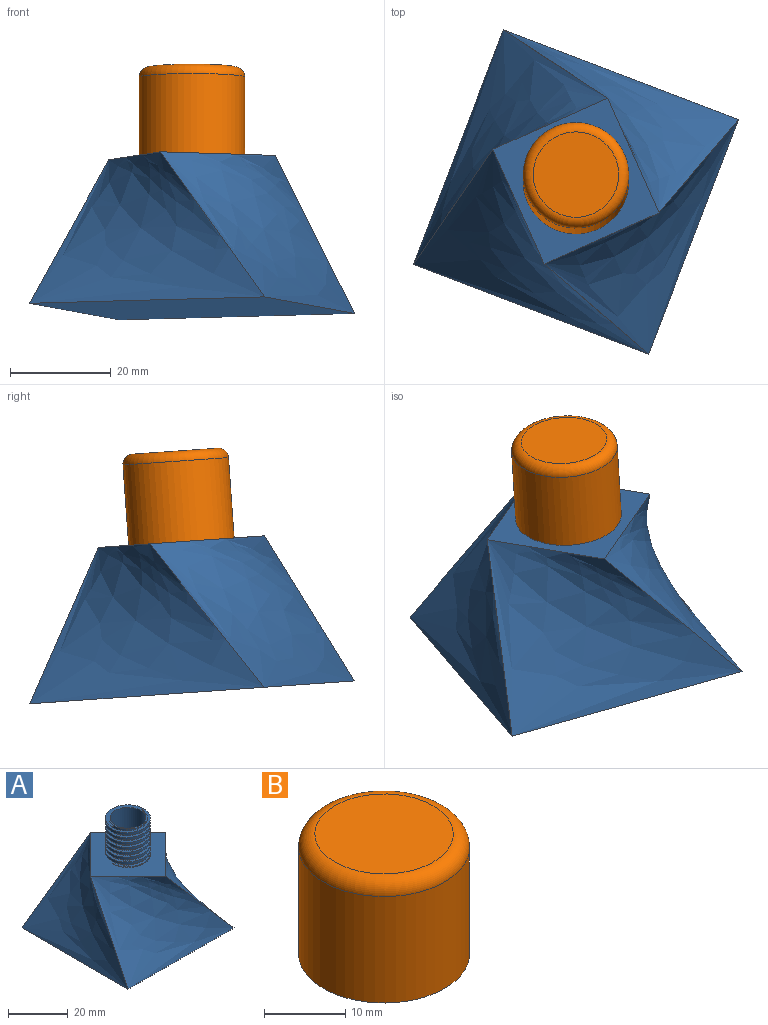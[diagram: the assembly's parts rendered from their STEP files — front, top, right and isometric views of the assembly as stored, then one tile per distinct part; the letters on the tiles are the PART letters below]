
ASSEMBLY  parts=2 mates=1
PART A: 18 faces, bbox 53x53x48 mm
  f0: cylinder r=7.5mm len=15mm, axis (0,0,-1), area 358.7mm2, adj f1,f3,f16,f17
  f1: plane 15x14mm, normal (0,0,1), area 41.6mm2, adj f0,f8,f15,f16,f17
  f2: plane 50x50mm, normal (0,0,-1), area 2500mm2, adj f4,f5,f6,f7
  f3: plane 35.36x35.36mm, normal (0,0,1), area 470.3mm2, adj f0,f4,f5,f6,f7,f15,f16,f17
  f4: bspline ~50x30mm, area 1200.4mm2, adj f2,f3,f5,f7
  f5: bspline ~50x30mm, area 1200.4mm2, adj f2,f3,f4,f6
  f6: bspline ~50x30mm, area 1200.4mm2, adj f2,f3,f5,f7
  f7: bspline ~50x30mm, area 1200.4mm2, adj f2,f3,f4,f6
  f8: cylinder r=6mm len=16.5mm, axis (0,0,-1), area 622mm2, adj f1,f10
  f9: plane 46.11x46.11mm, normal (0,0,1), area 2021.9mm2, adj f11,f12,f13,f14
  f10: plane 31.34x31.34mm, normal (0,0,-1), area 388.8mm2, adj f8,f11,f12,f13,f14
  f11: offset ~53x33mm, area 966.7mm2, adj f9,f10,f12,f14
  f12: offset ~53x33mm, area 966.7mm2, adj f9,f10,f11,f13
  f13: offset ~53x33mm, area 966.7mm2, adj f9,f10,f12,f14
  f14: offset ~53x33mm, area 966.7mm2, adj f9,f10,f11,f13
  f15: cylinder r=6.5mm len=15mm, axis (0,0,1), area 310.9mm2, adj f1,f3,f16,f17
  f16: bspline ~17.32x15.33mm, area 331.9mm2, adj f0,f1,f3,f15
  f17: bspline ~17.32x15.33mm, area 331.9mm2, adj f0,f1,f3,f15
PART B: 9 faces, bbox 22.7x22.7x18.3 mm
  f0: cylinder r=7.9mm len=15.8mm, axis (0,0,-1), area 377.8mm2, adj f1,f4,f6,f7
  f1: plane 15.8x14.8mm, normal (0,0,-1), area 172.8mm2, adj f0,f5,f6,f7
  f2: cylinder r=10.5mm len=21mm, axis (0,0,-1), area 1055.6mm2, adj f4,f8
  f3: plane 17x17mm, normal (0,0,1), area 227mm2, adj f8
  f4: plane 21x21mm, normal (0,0,-1), area 173.5mm2, adj f0,f2,f5,f6,f7
  f5: cylinder r=6.9mm len=15mm, axis (0,0,1), area 330mm2, adj f1,f4,f6,f7
  f6: bspline ~18.24x15.8mm, area 350.8mm2, adj f0,f1,f4,f5
  f7: bspline ~18.24x15.8mm, area 350.8mm2, adj f0,f1,f4,f5
  f8: torus R=8.5mm, axis (0,0,1), area 192.9mm2, adj f2,f3
PLACE A rot(axis=(-0.05,0.03,1),69.2deg) t=(24.69,33.65,17.53)mm
PLACE B rot(axis=(-0.53,-0.03,-0.85),7.6deg) t=(24.69,33.65,17.53)mm
MATE cylindrical B.f0 <-> A.f0  axis (0,-0.07,-1) through (24.68,36.81,62.42)mm
